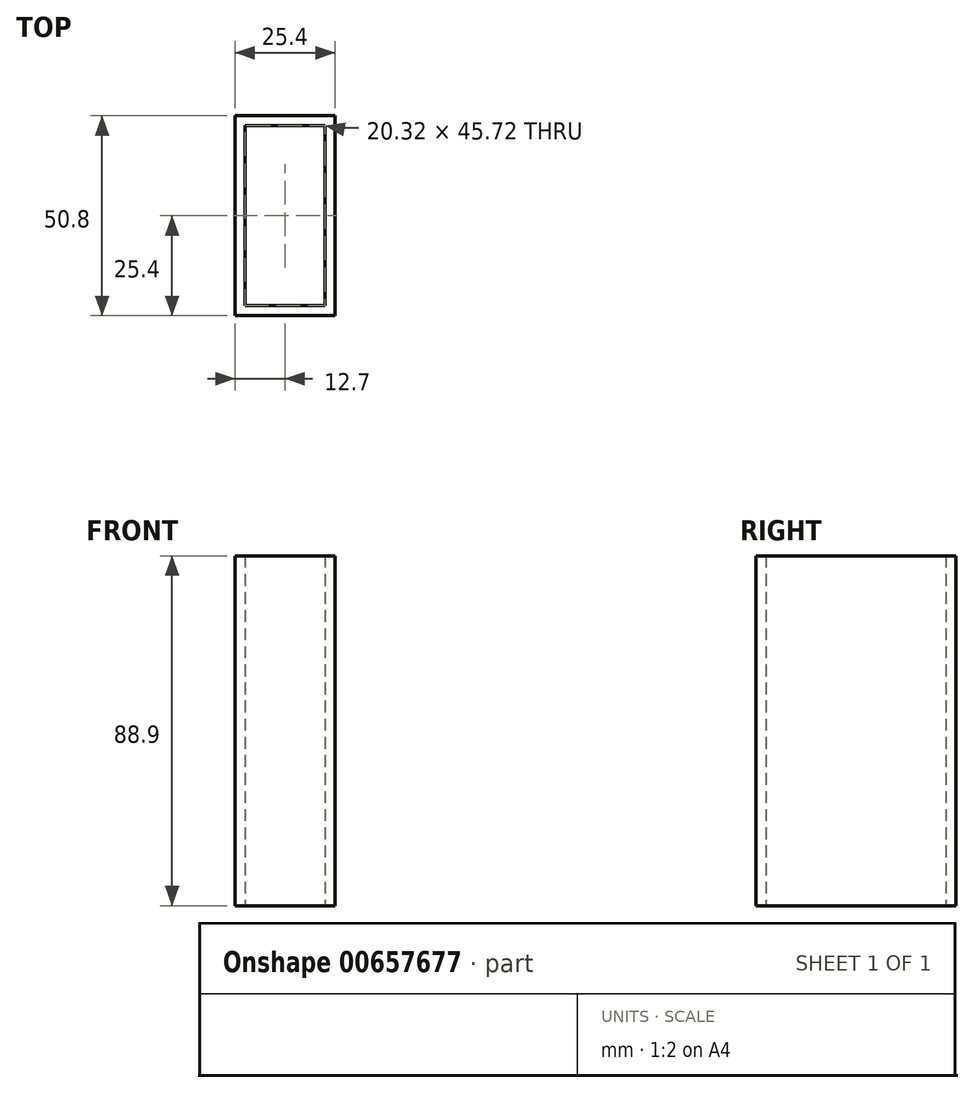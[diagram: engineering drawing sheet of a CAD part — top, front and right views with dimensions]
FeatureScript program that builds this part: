
annotation { "Feature Type Name" : "Feature", "Feature Type Description" : "" }
export const myFeature = defineFeature(function(context is Context, id is Id, definition is map)
    precondition{}
    {
        {
            var Q0;
            Q0=qCreatedBy(makeId("Top.planeOp"),FACE);
            var sketch = newSketch(context, id + "F0", { "sketchPlane" : qUnion([Q0])});
            skLineSegment(sketch, "E0.bottom", {"start": v(0, 0) * mm, "end": v(25.4, 0) * mm});
            skLineSegment(sketch, "E0.top", {"start": v(0, -50.8) * mm, "end": v(25.4, -50.8) * mm});
            skLineSegment(sketch, "E0.left", {"start": v(0, 0) * mm, "end": v(0, -50.8) * mm});
            skLineSegment(sketch, "E0.right", {"start": v(25.4, 0) * mm, "end": v(25.4, -50.8) * mm});
            skLineSegment(sketch, "E1.bottom", {"start": v(2.54, -48.26) * mm, "end": v(22.86, -48.26) * mm});
            skLineSegment(sketch, "E1.top", {"start": v(2.54, -2.54) * mm, "end": v(22.86, -2.54) * mm});
            skLineSegment(sketch, "E1.left", {"start": v(2.54, -48.26) * mm, "end": v(2.54, -2.54) * mm});
            skLineSegment(sketch, "E1.right", {"start": v(22.86, -48.26) * mm, "end": v(22.86, -2.54) * mm});
            skSolve(sketch);
        }
        {
            var Q0;
            Q0=makeQuery(id+"F0.imprint","IMPRINT",FACE,{"disambiguationData":[TD([[makeQuery(id+"F0.imprint","IMPRINT",EDGE,{"derivedFrom":sQuery(id+"F0.wireOp",EDGE,"E0.bottom")}),-1.0]])]});
            extrude(context, id + "F1", {"entities" : qUnion([Q0]), "depth" : 88.9 * mm, "offsetDistance" : 25.4 * mm});
        }
    });
